# Revit family: EdgeT1-F-RTB-2x2_family_2019_facehosted
name_source: partatom
category: Lighting Fixtures
revit_build: Autodesk Revit 2018 (Build: 20170223_1515(x64)
units: mm (PartAtom-declared; Revit-internal decimal feet)

## family parameters
Cut with Voids When Loaded = No
Host = Face
Light Source = Yes
Part Type = Normal
Room Calculation Point = No
Round Connector Dimension = Use Diameter
Shared = No

## types (3) — shared parameters
Color Filter = 16777215
Default Elevation = 4' - 0"
Dimming Lamp Color Temperature Shift = <None>
Housing Material = White Painted Aluminum
Illuminated Surface Material = Frosted Acrylic Lens
Tilt Angle = -90.00°
Voltage = 120 V

## per-type parameters (varying)
| type | Apparent Load | Photometric Web File |
| EdgeT1-F-RTB-2x2-250-B1-35K8-UNV-DM-W | 21 VA | EdgeT1-F-RTB-2x2-250-B1-35K8-UNV-DM-W.ies |
| EdgeT1-F-RTB-2x2-375-B1-35K8-UNV-DM-W | 29 VA | EdgeT1-F-RTB-2x2-375-B1-35K8-UNV-DM-W.ies |
| EdgeT1-F-RTB-2x2-500-B1-35K8-UNV-DM-W | 40 VA | EdgeT1-F-RTB-2x2-500-B1-35K8-UNV-DM-W.ies |

## geometry (parser evidence)
native form markers: Sweep x1
no freeform markers — native parametric forms only
